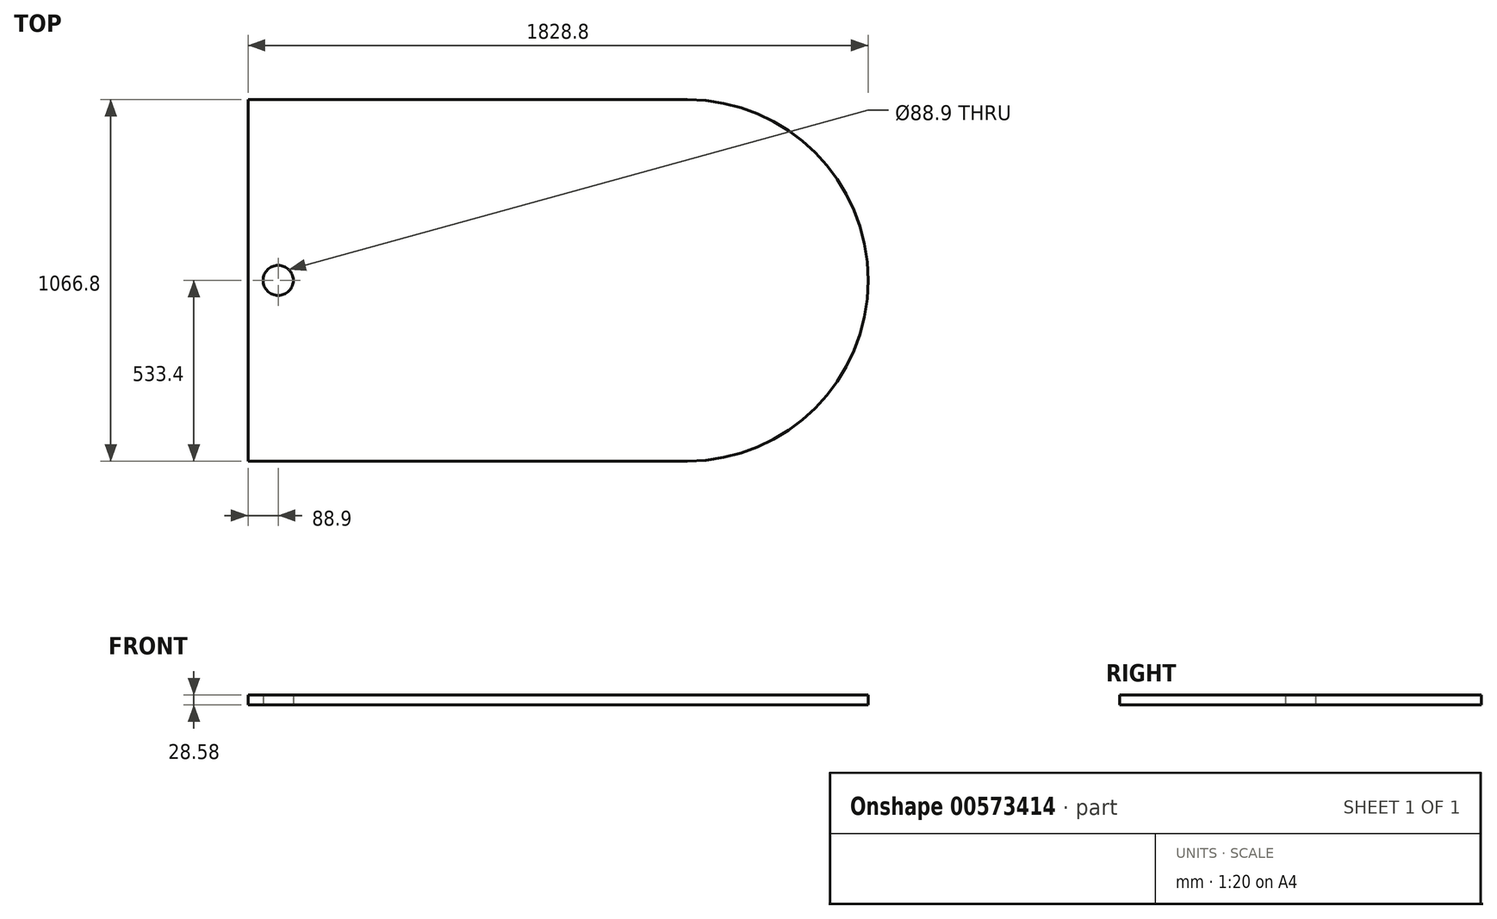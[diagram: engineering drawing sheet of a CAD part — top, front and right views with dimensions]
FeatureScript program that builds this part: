
annotation { "Feature Type Name" : "Feature", "Feature Type Description" : "" }
export const myFeature = defineFeature(function(context is Context, id is Id, definition is map)
    precondition{}
    {
        {
            var Q0;
            Q0=qCreatedBy(makeId("Top.planeOp"),FACE);
            var sketch = newSketch(context, id + "F0", { "sketchPlane" : qUnion([Q0])});
            skLineSegment(sketch, "E0.right", {"start": v(-990.6, 533.4) * mm, "end": v(-990.6, -533.4) * mm});
            skPoint(sketch, "E0.middle", {"position": v(0, 0) * mm});
            skLineSegment(sketch, "E1", {"start": v(-990.6, 0) * mm, "end": v(-901.7, 0) * mm});
            skPoint(sketch, "E1.endSnap0", {"position": v(-990.6, 0) * mm});
            skCircle(sketch, "E2", {"center": v(-901.7, 0) * mm, "radius": 44.45 * mm});
            skLineSegment(sketch, "E3", {"start": v(838.2, 0) * mm, "end": v(304.8, 0) * mm});
            skArc(sketch, "E4", {"start": v(838.2, 0) * mm, "mid": v(681.97, 377.17) * mm, "end": v(304.8, 533.4) * mm});
            skArc(sketch, "E5", {"start": v(838.2, 0) * mm, "mid": v(681.97, -377.17) * mm, "end": v(304.8, -533.4) * mm});
            skLineSegment(sketch, "E6", {"start": v(304.8, 533.4) * mm, "end": v(-990.6, 533.4) * mm});
            skLineSegment(sketch, "E7", {"start": v(-990.6, -533.4) * mm, "end": v(304.8, -533.4) * mm});
            skSolve(sketch);
        }
        {
            var Q0;
            {var subQ1=sQuery(id+"F0.wireOp",EDGE,"E0.bottom");Q0=makeQuery(id+"F0.imprint","IMPRINT",FACE,{"disambiguationData":[TD([[makeQuery(id+"F0.imprint","IMPRINT",EDGE,{"derivedFrom":subQ1}),1.0]])]});}
            var Q1;
            Q1=makeQuery(id+"F0.imprint","IMPRINT",FACE,{"disambiguationData":[TD([[makeQuery(id+"F0.imprint","IMPRINT",EDGE,{"derivedFrom":sQuery(id+"F0.wireOp",EDGE,"E2")}),-1.0]])]});
            extrude(context, id + "F1", {"entities" : qUnion([Q0, Q1]), "depth" : 28.57 * mm, "offsetDistance" : 25.4 * mm});
        }
    });
